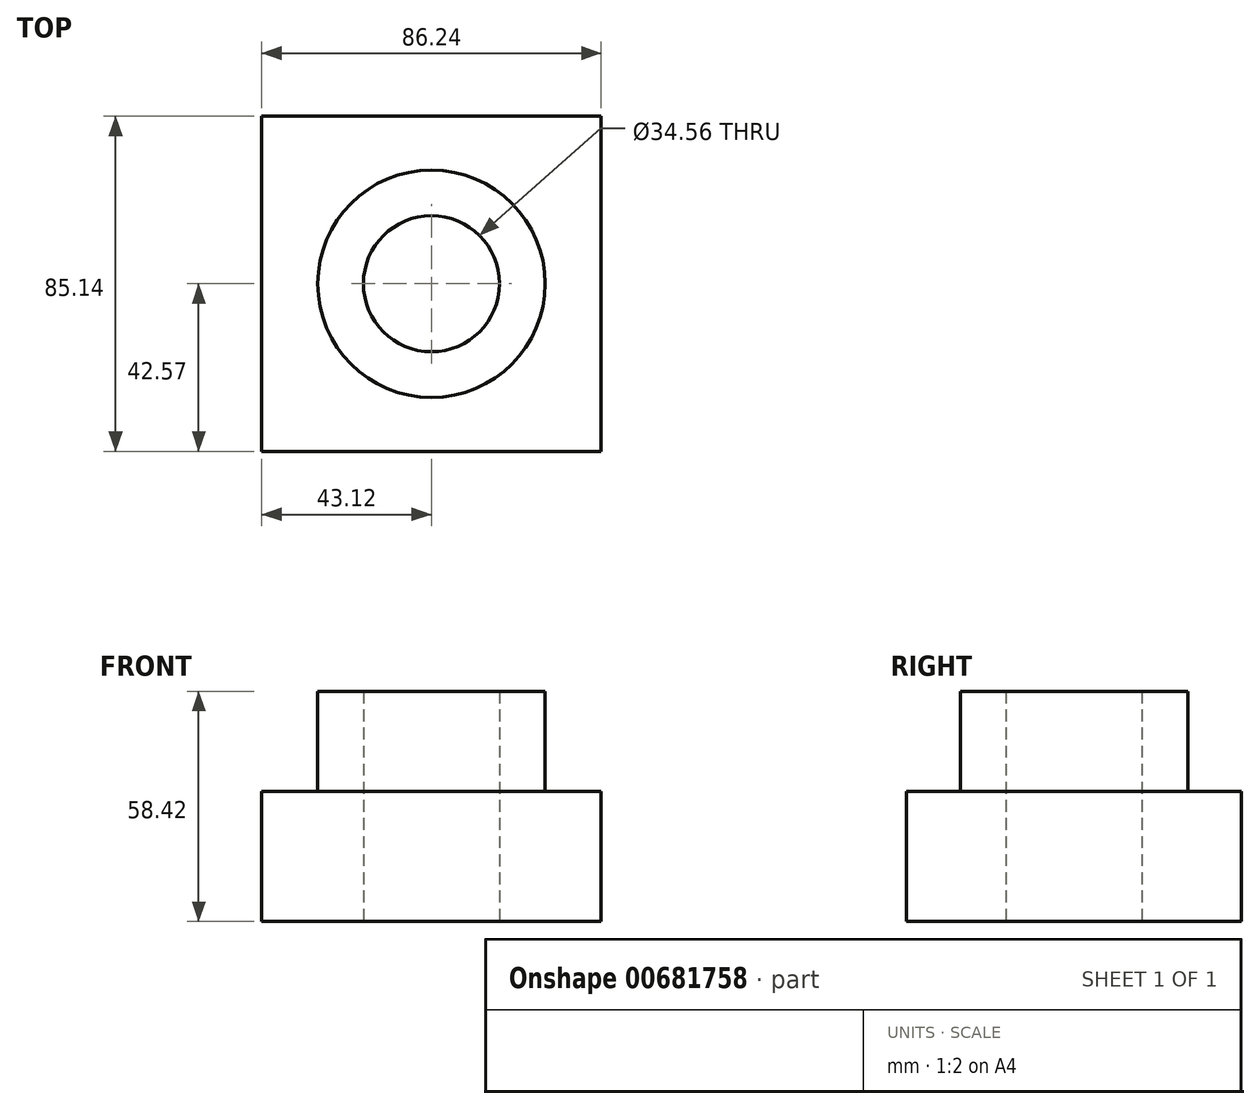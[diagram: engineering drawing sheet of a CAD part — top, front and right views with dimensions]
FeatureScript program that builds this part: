
annotation { "Feature Type Name" : "Feature", "Feature Type Description" : "" }
export const myFeature = defineFeature(function(context is Context, id is Id, definition is map)
    precondition{}
    {
        {
            var Q0;
            Q0=qCreatedBy(makeId("Top.planeOp"),FACE);
            var sketch = newSketch(context, id + "F0", { "sketchPlane" : qUnion([Q0])});
            skLineSegment(sketch, "E0.bottom", {"start": v(43.12, -42.57) * mm, "end": v(-43.12, -42.57) * mm});
            skLineSegment(sketch, "E0.top", {"start": v(43.12, 42.57) * mm, "end": v(-43.12, 42.57) * mm});
            skLineSegment(sketch, "E0.left", {"start": v(43.12, -42.57) * mm, "end": v(43.12, 42.57) * mm});
            skLineSegment(sketch, "E0.right", {"start": v(-43.12, -42.57) * mm, "end": v(-43.12, 42.57) * mm});
            skPoint(sketch, "E0.middle", {"position": v(0, 0) * mm});
            skSolve(sketch);
        }
        {
            var Q0;
            Q0 = qSketchRegion(id + "F0", true);
            extrude(context, id + "F1", {"entities" : qUnion([Q0]), "depth" : 33.02 * mm, "offsetDistance" : 25.4 * mm});
        }
        {
            var Q0;
            Q0=makeQuery(id+"F1.opExtrude","CAP_FACE",FACE,{"disambiguationData":[OSD([sQuery(id+"F0.wireOp",EDGE,"E0.bottom"),sQuery(id+"F0.wireOp",EDGE,"E0.top"),sQuery(id+"F0.wireOp",EDGE,"E0.left"),sQuery(id+"F0.wireOp",EDGE,"E0.right")])],"isStart":false});
            var sketch = newSketch(context, id + "F2", { "sketchPlane" : qUnion([Q0])});
            skCircle(sketch, "E1", {"center": v(0, 0) * mm, "radius": 28.89 * mm});
            skCircle(sketch, "E2", {"center": v(0, 0) * mm, "radius": 17.28 * mm});
            skSolve(sketch);
        }
        {
            var Q0;
            Q0 = qSketchRegion(id + "F2", true);
            extrude(context, id + "F3", {"entities" : qUnion([Q0]), "operationType" : NewBodyOperationType.ADD, "depth" : 25.4 * mm, "offsetDistance" : 25.4 * mm});
        }
        {
            var Q0;
            Q0=makeQuery(id+"F3.boolean.opBoolean","SPLIT",FACE,{"disambiguationData":[TD([makeQuery(id+"F3.opExtrude","SWEPT_FACE",FACE,{"disambiguationData":[OSD([sQuery(id+"F2.wireOp",EDGE,"E2")])]})])],"derivedFrom":makeQuery(id+"F1.opExtrude","CAP_FACE",FACE,{"disambiguationData":[OSD([sQuery(id+"F0.wireOp",EDGE,"E0.bottom"),sQuery(id+"F0.wireOp",EDGE,"E0.top"),sQuery(id+"F0.wireOp",EDGE,"E0.left"),sQuery(id+"F0.wireOp",EDGE,"E0.right")])],"isStart":false})});
            extrude(context, id + "F4", {"entities" : qUnion([Q0]), "operationType" : NewBodyOperationType.REMOVE, "oppositeDirection" : true, "depth" : 127 * mm, "offsetDistance" : 25.4 * mm});
        }
    });
